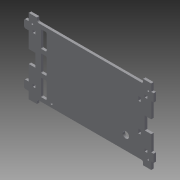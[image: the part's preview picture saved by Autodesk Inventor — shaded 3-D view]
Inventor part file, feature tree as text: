
AUTODESK INVENTOR PART (.ipt)
format: ipt  version: 2015 (Build 190159000, 159)  size: 283,136 bytes
history: native  units: mm
features: extrude x3, sketch x3
ambient origin geometry x8: Origin, YZ Plane, XZ Plane, XY Plane, X Axis, Y Axis, Z Axis, Center Point
bodies: Solid1 (feature_tree)
feature tree (6):
  extrude  "Extrusion1"  Depth=3.0mm
  extrude  "Extrusion5"  Depth=8.0mm
  extrude  "Extrusion8"  Depth=3.0mm
  sketch  "Sketch1"  dims[d5=10.0mm d20=3.0mm]
  sketch  "Sketch2"  dims[d42=47.0mm d43=3.0mm d44=8.0mm]
  sketch  "Sketch4"  dims[d45=81.0mm d47=3.0mm d49=10.0mm d50=10.0mm d52=3.0mm d53=6.0mm d54=6.0mm d56=5.0mm d57=5.0mm d58=85.0mm d59=3.0mm d60=0.0mm d61=93.0mm d63=19.5mm d65=9.5mm d74=2.0mm d75=8.0mm d76=8.0mm d77=16.0mm d78=36.5mm d79=3.0mm d80=3.0mm d81=3.0mm d82=3.0mm d83=5.0mm d84=5.0mm d85=27.5mm d86=27.5mm d89=8.0mm d90=5.0mm d91=5.0mm d92=27.5mm d93=27.5mm d94=3.0mm d95=3.0mm d96=3.0mm d97=3.0mm d113=5.0mm d114=10.0mm d115=10.0mm d116=5.0mm d117=10.0mm d118=10.0mm d119=2.0mm d120=6.0mm d124=41.5mm d127=6.0mm d128=80.0mm d129=3.0mm d130=132.0mm d133=3.0mm d135=33.0mm d136=93.0mm d140=16.0mm d142=8.0mm d144=10.0mm d145=5.0mm d146=5.0mm d147=27.5mm d148=27.5mm d149=27.5mm d150=27.5mm d151=5.0mm d152=3.0mm d153=5.0mm d154=3.0mm d155=30.0mm d159=10.0mm d160=0.0mm d161=16.0mm d162=16.0mm d164=161.0mm d165=31.5mm d167=17.0mm d168=8.0mm d169=3.0mm d170=3.0mm d171=144.0mm d172=4.0mm d173=31.5mm d176=3.0mm d177=74.0mm d179=4.5mm d181=4.5mm d184=4.5mm d185=21.0mm d186=7.0mm d187=15.0mm d188=5.0mm d189=21.0mm d190=7.0mm d191=5.0mm d192=15.0mm d193=21.0mm d194=5.0mm d195=15.0mm d196=7.0mm d197=1.0mm d200=3.0mm d201=4.5mm d202=24.0mm d203=10.0mm d204=0.0mm]
